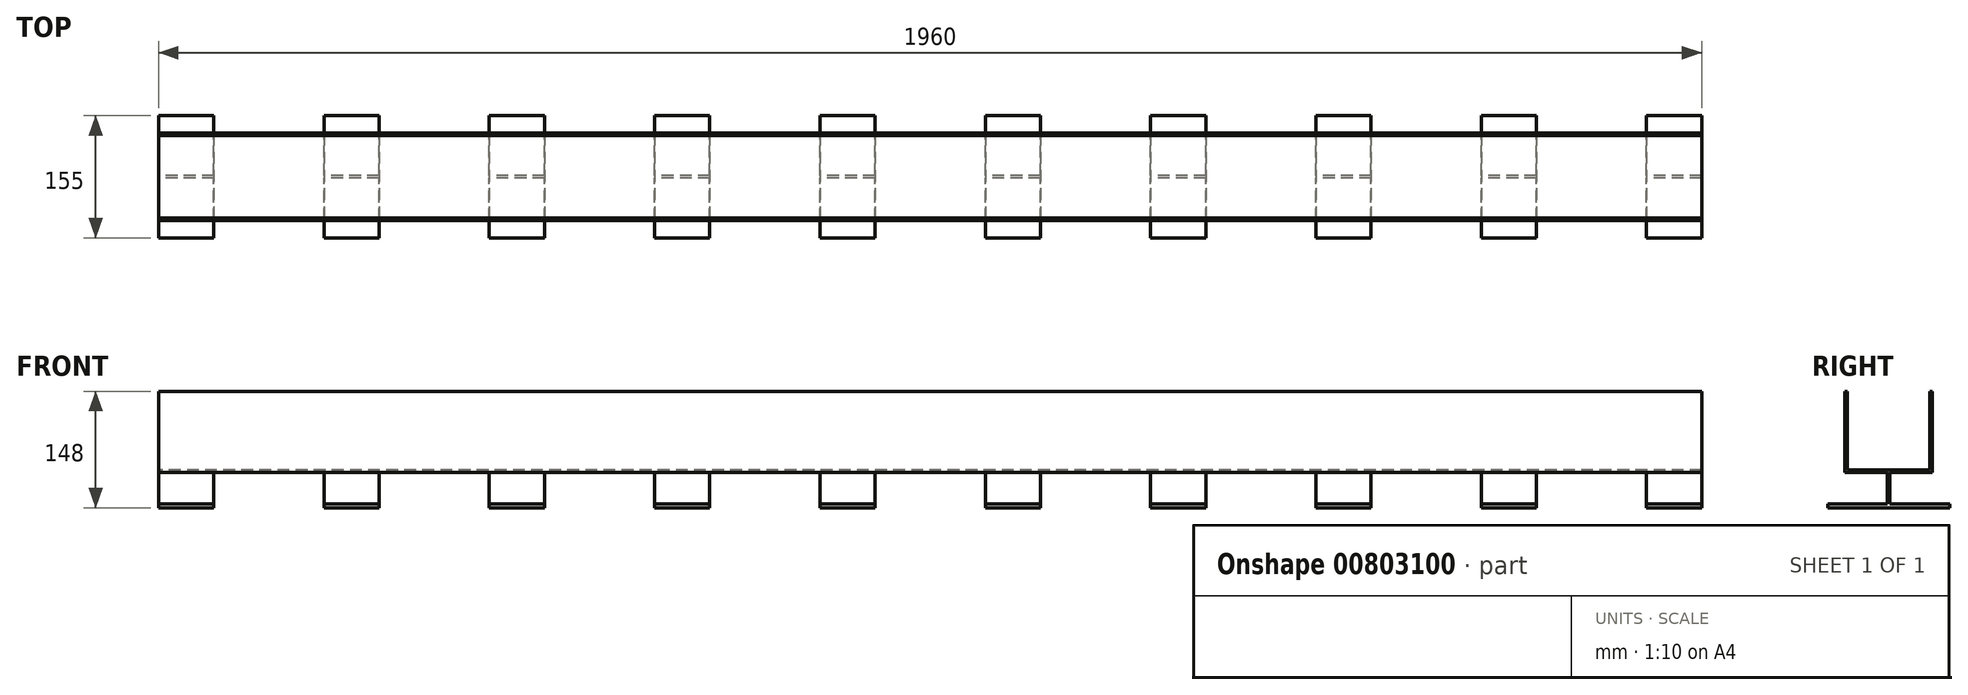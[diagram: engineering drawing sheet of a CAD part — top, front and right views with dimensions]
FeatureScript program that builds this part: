
annotation { "Feature Type Name" : "Feature", "Feature Type Description" : "" }
export const myFeature = defineFeature(function(context is Context, id is Id, definition is map)
    precondition{}
    {
        {
            var Q0;
            Q0=qCreatedBy(makeId("Right.planeOp"),FACE);
            var sketch = newSketch(context, id + "F0", { "sketchPlane" : qUnion([Q0])});
            skLineSegment(sketch, "E0.top", {"start": v(3, 3) * mm, "end": v(108, 3) * mm});
            skLineSegment(sketch, "E0.left", {"start": v(3, 103) * mm, "end": v(3, 3) * mm});
            skLineSegment(sketch, "E0.right", {"start": v(108, 103) * mm, "end": v(108, 3) * mm});
            skLineSegment(sketch, "E1.0", {"start": v(0, 103) * mm, "end": v(0, 0) * mm});
            skLineSegment(sketch, "E2.0", {"start": v(0, 0) * mm, "end": v(54, 0) * mm});
            skLineSegment(sketch, "E3.0", {"start": v(111, 103) * mm, "end": v(111, 0) * mm});
            skLineSegment(sketch, "E4", {"start": v(3, 103) * mm, "end": v(0, 103) * mm});
            skLineSegment(sketch, "E5", {"start": v(108, 103) * mm, "end": v(111, 103) * mm});
            skLineSegment(sketch, "E6", {"start": v(57, -40) * mm, "end": v(57, 0) * mm});
            skLineSegment(sketch, "E7", {"start": v(54, 0) * mm, "end": v(54, -40) * mm});
            skLineSegment(sketch, "E8.trimOffspring", {"start": v(57, 0) * mm, "end": v(111, 0) * mm});
            skLineSegment(sketch, "E9.bottom", {"start": v(-22, -40) * mm, "end": v(54, -40) * mm});
            skLineSegment(sketch, "E9.top", {"start": v(-22, -45) * mm, "end": v(133, -45) * mm});
            skLineSegment(sketch, "E9.left", {"start": v(-22, -40) * mm, "end": v(-22, -45) * mm});
            skLineSegment(sketch, "E9.right", {"start": v(133, -40) * mm, "end": v(133, -45) * mm});
            skLineSegment(sketch, "E10.trimOffspring", {"start": v(57, -40) * mm, "end": v(133, -40) * mm});
            skPoint(sketch, "E11.orphan", {"position": v(55.5, -40) * mm});
            skSolve(sketch);
        }
        {
            var Q0;
            Q0=makeQuery(id+"F0.imprint","IMPRINT",FACE,{"disambiguationData":[TD([[makeQuery(id+"F0.imprint","IMPRINT",EDGE,{"derivedFrom":sQuery(id+"F0.wireOp",EDGE,"E0.top")}),-1.0]])]});
            extrude(context, id + "F1", {"entities" : qUnion([Q0]), "depth" : 3285 * mm, "offsetDistance" : 25 * mm});
        }
        {
            var Q0;
            Q0=makeQuery(id+"F1.opExtrude","SWEPT_FACE",FACE,{"disambiguationData":[OSD([sQuery(id+"F0.wireOp",EDGE,"E9.left")])]});
            var sketch = newSketch(context, id + "F2", { "sketchPlane" : qUnion([Q0])});
            skLineSegment(sketch, "E12.bottom", {"start": v(70, -45) * mm, "end": v(210, -45) * mm});
            skLineSegment(sketch, "E12.top", {"start": v(70, 0) * mm, "end": v(210, 0) * mm});
            skLineSegment(sketch, "E12.left", {"start": v(70, -45) * mm, "end": v(70, 0) * mm});
            skLineSegment(sketch, "E12.right", {"start": v(210, -45) * mm, "end": v(210, 0) * mm});
            skLineSegment(sketch, "E13.bottom", {"start": v(280, -45) * mm, "end": v(420, -45) * mm});
            skLineSegment(sketch, "E13.top", {"start": v(280, 0) * mm, "end": v(420, 0) * mm});
            skLineSegment(sketch, "E13.left", {"start": v(280, -45) * mm, "end": v(280, 0) * mm});
            skLineSegment(sketch, "E13.right", {"start": v(420, -45) * mm, "end": v(420, 0) * mm});
            skLineSegment(sketch, "E14.bottom", {"start": v(490, -45) * mm, "end": v(630, -45) * mm});
            skLineSegment(sketch, "E14.top", {"start": v(490, 0) * mm, "end": v(630, 0) * mm});
            skLineSegment(sketch, "E14.left", {"start": v(490, -45) * mm, "end": v(490, 0) * mm});
            skLineSegment(sketch, "E14.right", {"start": v(630, -45) * mm, "end": v(630, 0) * mm});
            skLineSegment(sketch, "E15.bottom", {"start": v(700, -45) * mm, "end": v(840, -45) * mm});
            skLineSegment(sketch, "E15.top", {"start": v(700, 0) * mm, "end": v(840, 0) * mm});
            skLineSegment(sketch, "E15.left", {"start": v(700, -45) * mm, "end": v(700, 0) * mm});
            skLineSegment(sketch, "E15.right", {"start": v(840, -45) * mm, "end": v(840, 0) * mm});
            skLineSegment(sketch, "E16.bottom", {"start": v(910, -45) * mm, "end": v(1050, -45) * mm});
            skLineSegment(sketch, "E16.top", {"start": v(910, 0) * mm, "end": v(1050, 0) * mm});
            skLineSegment(sketch, "E16.left", {"start": v(910, -45) * mm, "end": v(910, 0) * mm});
            skLineSegment(sketch, "E16.right", {"start": v(1050, -45) * mm, "end": v(1050, 0) * mm});
            skLineSegment(sketch, "E17.bottom", {"start": v(1120, -45) * mm, "end": v(1260, -45) * mm});
            skLineSegment(sketch, "E17.top", {"start": v(1120, 0) * mm, "end": v(1260, 0) * mm});
            skLineSegment(sketch, "E17.left", {"start": v(1120, -45) * mm, "end": v(1120, 0) * mm});
            skLineSegment(sketch, "E17.right", {"start": v(1260, -45) * mm, "end": v(1260, 0) * mm});
            skLineSegment(sketch, "E18.bottom", {"start": v(1330, -45) * mm, "end": v(1470, -45) * mm});
            skLineSegment(sketch, "E18.top", {"start": v(1330, 0) * mm, "end": v(1470, 0) * mm});
            skLineSegment(sketch, "E18.left", {"start": v(1330, -45) * mm, "end": v(1330, 0) * mm});
            skLineSegment(sketch, "E18.right", {"start": v(1470, -45) * mm, "end": v(1470, 0) * mm});
            skLineSegment(sketch, "E19.bottom", {"start": v(1540, -45) * mm, "end": v(1680, -45) * mm});
            skLineSegment(sketch, "E19.top", {"start": v(1540, 0) * mm, "end": v(1680, 0) * mm});
            skLineSegment(sketch, "E19.left", {"start": v(1540, -45) * mm, "end": v(1540, 0) * mm});
            skLineSegment(sketch, "E19.right", {"start": v(1680, -45) * mm, "end": v(1680, 0) * mm});
            skLineSegment(sketch, "E20.bottom", {"start": v(1750, -45) * mm, "end": v(1890, -45) * mm});
            skLineSegment(sketch, "E20.top", {"start": v(1750, 0) * mm, "end": v(1890, 0) * mm});
            skLineSegment(sketch, "E20.left", {"start": v(1750, -45) * mm, "end": v(1750, 0) * mm});
            skLineSegment(sketch, "E20.right", {"start": v(1890, -45) * mm, "end": v(1890, 0) * mm});
            skLineSegment(sketch, "E21", {"start": v(1890, -22.5) * mm, "end": v(1960, -22.5) * mm});
            skLineSegment(sketch, "E22.bottom", {"start": v(1960, -45) * mm, "end": v(3285, -45) * mm});
            skLineSegment(sketch, "E22.top", {"start": v(1960, 103) * mm, "end": v(3285, 103) * mm});
            skLineSegment(sketch, "E22.left", {"start": v(1960, -45) * mm, "end": v(1960, 103) * mm});
            skLineSegment(sketch, "E22.right", {"start": v(3285, -45) * mm, "end": v(3285, 103) * mm});
            skSolve(sketch);
        }
        {
            var Q0;
            Q0 = qSketchRegion(id + "F2", true);
            var Q1;
            Q1=makeQuery(id+"F1.opExtrude","SWEPT_FACE",FACE,{"disambiguationData":[OSD([sQuery(id+"F0.wireOp",EDGE,"E9.right")])]});
            extrude(context, id + "F3", {"entities" : qUnion([Q0]), "operationType" : NewBodyOperationType.REMOVE, "endBound" : BoundingType.UP_TO_SURFACE, "oppositeDirection" : true, "depth" : 25 * mm, "endBoundEntityFace" : qUnion([Q1]), "offsetDistance" : 25 * mm});
        }
    });
